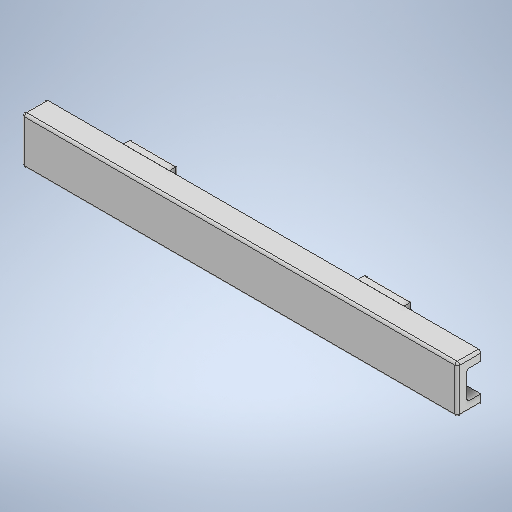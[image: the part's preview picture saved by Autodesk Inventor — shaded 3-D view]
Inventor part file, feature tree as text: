
AUTODESK INVENTOR PART (.ipt)
format: ipt  version: 2025 (Build 290162000, 162)  size: 326,656 bytes
history: native  units: mm
features: extrude x3, sketch x3, fillet x1
ambient origin geometry x8: Origin, YZ Plane, XZ Plane, XY Plane, X Axis, Y Axis, Z Axis, Center Point
bodies: Volumenkörper1 (feature_tree)
feature tree (7):
  extrude  "Extrusion1"  Depth=185.0mm
  extrude  "Extrusion2"  Depth=4.0mm
  extrude  "Extrusion3"  Depth=4.0mm
  fillet  "Rundung1"  Radius=181.0mm
  sketch  "Skizze1"  dims[d0=20.0mm d1=185.0mm]
  sketch  "Skizze2"  dims[d2=10.0mm d3=0.0mm d4=4.0mm]
  sketch  "Skizze3"  dims[d5=4.0mm d6=4.0mm d7=181.0mm d8=0.0mm d9=3.5mm d10=32.85mm d11=0.25mm d12=19.6mm d13=0.25mm d14=3.5mm d15=32.85mm d16=0.25mm d17=19.6mm d18=3.5mm d19=0.25mm d20=3.5mm d21=3.925mm d22=0.0mm d23=0.0mm d24=0.0mm d25=1.0mm]
